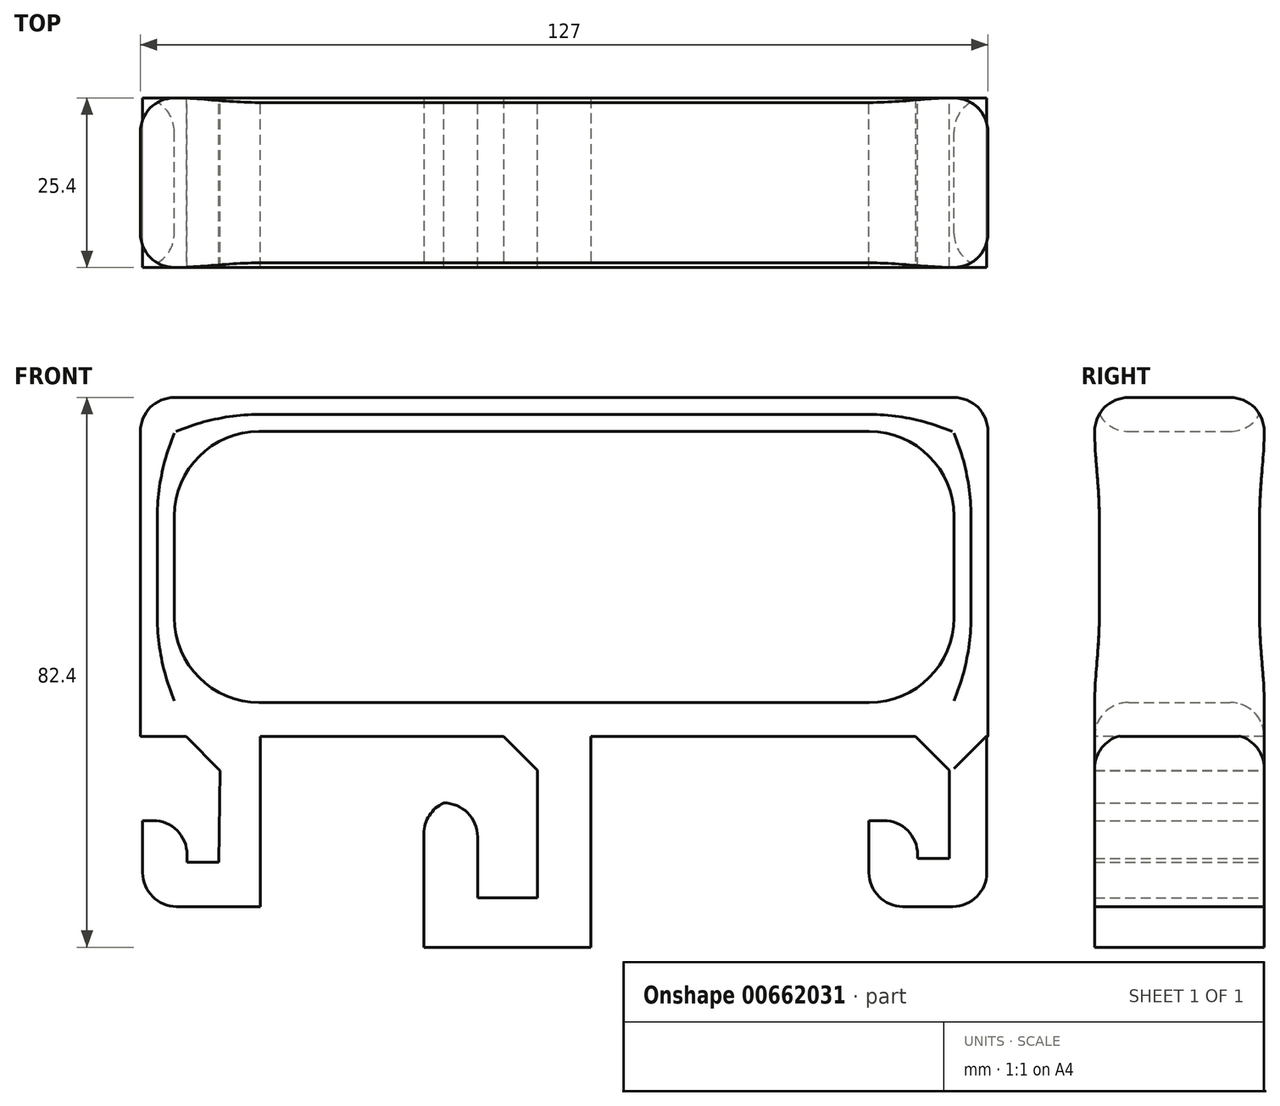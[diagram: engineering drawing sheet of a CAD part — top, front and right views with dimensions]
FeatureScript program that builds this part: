
annotation { "Feature Type Name" : "Feature", "Feature Type Description" : "" }
export const myFeature = defineFeature(function(context is Context, id is Id, definition is map)
    precondition{}
    {
        {
            var Q0;
            Q0=qCreatedBy(makeId("Front.planeOp"),FACE);
            var sketch = newSketch(context, id + "F0", { "sketchPlane" : qUnion([Q0])});
            skLineSegment(sketch, "E0.bottom", {"start": v(-63.5, -25.4) * mm, "end": v(63.5, -25.4) * mm});
            skLineSegment(sketch, "E0.top", {"start": v(-63.5, 25.4) * mm, "end": v(63.5, 25.4) * mm});
            skLineSegment(sketch, "E0.left", {"start": v(-63.5, -25.4) * mm, "end": v(-63.5, 25.4) * mm});
            skLineSegment(sketch, "E0.right", {"start": v(63.5, -25.4) * mm, "end": v(63.5, 25.4) * mm});
            skPoint(sketch, "E0.middle", {"position": v(0, 0) * mm});
            skSolve(sketch);
        }
        {
            var Q0;
            Q0=makeQuery(id+"F0.imprint","IMPRINT",FACE,{"disambiguationData":[TD([[makeQuery(id+"F0.imprint","IMPRINT",EDGE,{"derivedFrom":sQuery(id+"F0.wireOp",EDGE,"E0.bottom")}),1.0]])]});
            extrude(context, id + "F1", {"entities" : qUnion([Q0]), "depth" : 25.4 * mm, "offsetDistance" : 25.4 * mm});
        }
        {
            var Q0;
            Q0=makeQuery(id+"F1.opExtrude","CAP_FACE",FACE,{"disambiguationData":[OSD([sQuery(id+"F0.wireOp",EDGE,"E0.bottom"),sQuery(id+"F0.wireOp",EDGE,"E0.top"),sQuery(id+"F0.wireOp",EDGE,"E0.left"),sQuery(id+"F0.wireOp",EDGE,"E0.right")])],"isStart":true});
            var Q1;
            Q1=makeQuery(id+"F1.opExtrude","CAP_FACE",FACE,{"disambiguationData":[OSD([sQuery(id+"F0.wireOp",EDGE,"E0.bottom"),sQuery(id+"F0.wireOp",EDGE,"E0.top"),sQuery(id+"F0.wireOp",EDGE,"E0.left"),sQuery(id+"F0.wireOp",EDGE,"E0.right")])],"isStart":false});
            shell(context, id + "F2", {"entities" : qUnion([Q0, Q1]), "thickness" : 5.08 * mm});
        }
        {
            var Q0;
            Q0=makeQuery(id+"F2.opShell","OFFSET_EDGE",EDGE,{"disambiguationData":[OSD([sQuery(id+"F0.wireOp",EDGE,"E0.bottom"),sQuery(id+"F0.wireOp",EDGE,"E0.right")])]});
            var Q1;
            Q1=makeQuery(id+"F2.opShell","OFFSET_EDGE",EDGE,{"disambiguationData":[OSD([sQuery(id+"F0.wireOp",EDGE,"E0.top"),sQuery(id+"F0.wireOp",EDGE,"E0.right")])]});
            var Q2;
            Q2=makeQuery(id+"F2.opShell","OFFSET_EDGE",EDGE,{"disambiguationData":[OSD([sQuery(id+"F0.wireOp",EDGE,"E0.bottom"),sQuery(id+"F0.wireOp",EDGE,"E0.left")])]});
            var Q3;
            Q3=makeQuery(id+"F2.opShell","OFFSET_EDGE",EDGE,{"disambiguationData":[OSD([sQuery(id+"F0.wireOp",EDGE,"E0.top"),sQuery(id+"F0.wireOp",EDGE,"E0.left")])]});
            fillet(context, id + "F3", {"entities" : qUnion([Q0, Q1, Q2, Q3]), "radius" : 12.7 * mm, "tangentPropagation" : true, "allowEdgeOverflow" : false});
        }
        {
            var Q0;
            Q0=makeQuery(id+"F1.opExtrude","SWEPT_EDGE",EDGE,{"disambiguationData":[OSD([sQuery(id+"F0.wireOp",EDGE,"E0.top"),sQuery(id+"F0.wireOp",EDGE,"E0.right")])]});
            var Q1;
            Q1=makeQuery(id+"F1.opExtrude","SWEPT_EDGE",EDGE,{"disambiguationData":[OSD([sQuery(id+"F0.wireOp",EDGE,"E0.top"),sQuery(id+"F0.wireOp",EDGE,"E0.left")])]});
            fillet(context, id + "F4", {"entities" : qUnion([Q0, Q1]), "radius" : 5.08 * mm, "tangentPropagation" : true, "allowEdgeOverflow" : false});
        }
        {
            var Q0;
            {var subQ0=sQuery(id+"F0.wireOp",EDGE,"E0.top");Q0=makeQuery(id+"F2.opShell","OFFSET_EDGE",EDGE,{"disambiguationData":[OSD([subQ0]),TDD([makeQuery(id+"F1.opExtrude","CAP_EDGE",EDGE,{"disambiguationData":[OSD([subQ0])],"isStart":true})])]});}
            var Q1;
            Q1=makeQuery(id+"F1.opExtrude","CAP_EDGE",EDGE,{"disambiguationData":[OSD([sQuery(id+"F0.wireOp",EDGE,"E0.top")])],"isStart":true});
            var Q2;
            {var subQ0=sQuery(id+"F0.wireOp",EDGE,"E0.top");Q2=makeQuery(id+"F2.opShell","OFFSET_EDGE",EDGE,{"disambiguationData":[OSD([subQ0]),TDD([makeQuery(id+"F1.opExtrude","CAP_EDGE",EDGE,{"disambiguationData":[OSD([subQ0])],"isStart":false})])]});}
            var Q3;
            Q3=makeQuery(id+"F1.opExtrude","CAP_EDGE",EDGE,{"disambiguationData":[OSD([sQuery(id+"F0.wireOp",EDGE,"E0.top")])],"isStart":false});
            fillet(context, id + "F5", {"entities" : qUnion([Q0, Q1, Q2, Q3]), "radius" : 5.08 * mm, "tangentPropagation" : true, "allowEdgeOverflow" : false});
        }
        {
            var Q0;
            Q0=qCreatedBy(makeId("Front.planeOp"),FACE);
            var sketch = newSketch(context, id + "F6", { "sketchPlane" : qUnion([Q0])});
            skLineSegment(sketch, "E1.bottom", {"start": v(63.32, -25.15) * mm, "end": v(45.68, -25.15) * mm});
            skLineSegment(sketch, "E1.top", {"start": v(63.32, -50.9) * mm, "end": v(45.68, -50.9) * mm});
            skLineSegment(sketch, "E1.left", {"start": v(63.32, -25.15) * mm, "end": v(63.32, -50.9) * mm});
            skLineSegment(sketch, "E1.right", {"start": v(45.68, -25.15) * mm, "end": v(45.68, -50.9) * mm});
            skLineSegment(sketch, "E2.bottom", {"start": v(-63.16, -25.15) * mm, "end": v(-45.52, -25.15) * mm});
            skLineSegment(sketch, "E2.top", {"start": v(-63.16, -50.9) * mm, "end": v(-45.52, -50.9) * mm});
            skLineSegment(sketch, "E2.left", {"start": v(-63.16, -25.15) * mm, "end": v(-63.16, -50.9) * mm});
            skLineSegment(sketch, "E2.right", {"start": v(-45.52, -25.15) * mm, "end": v(-45.52, -50.9) * mm});
            skLineSegment(sketch, "E3", {"start": v(45.68, -50.9) * mm, "end": v(45.68, -38.03) * mm});
            skLineSegment(sketch, "E4", {"start": v(45.68, -38.03) * mm, "end": v(52.97, -38.03) * mm});
            skLineSegment(sketch, "E5", {"start": v(52.97, -38.03) * mm, "end": v(52.97, -43.67) * mm});
            skLineSegment(sketch, "E6", {"start": v(52.97, -43.67) * mm, "end": v(57.71, -43.67) * mm});
            skLineSegment(sketch, "E7", {"start": v(57.71, -43.67) * mm, "end": v(57.71, -25.15) * mm});
            skLineSegment(sketch, "E8", {"start": v(-63.16, -38.03) * mm, "end": v(-56.5, -38.03) * mm});
            skLineSegment(sketch, "E9", {"start": v(-56.5, -38.03) * mm, "end": v(-56.5, -44.26) * mm});
            skLineSegment(sketch, "E10", {"start": v(-56.5, -44.26) * mm, "end": v(-51.76, -44.26) * mm});
            skLineSegment(sketch, "E11", {"start": v(-51.76, -44.26) * mm, "end": v(-49.1, -25.15) * mm});
            skLineSegment(sketch, "E12", {"start": v(-49.1, -25.15) * mm, "end": v(-51.46, -25.15) * mm});
            skLineSegment(sketch, "E13", {"start": v(-51.46, -25.15) * mm, "end": v(-51.76, -44.26) * mm});
            skLineSegment(sketch, "E14", {"start": v(-51.46, -25.15) * mm, "end": v(-45.52, -25.15) * mm});
            skSolve(sketch);
        }
        {
            var Q0;
            {var subQ2=sQuery(id+"F6.wireOp",EDGE,"E2.top");Q0=makeQuery(id+"F6.imprint","IMPRINT",FACE,{"disambiguationData":[TD([[makeQuery(id+"F6.imprint","IMPRINT",EDGE,{"derivedFrom":subQ2}),1.0]])]});}
            var Q1;
            {var subQ0=sQuery(id+"F6.wireOp",EDGE,"E11");Q1=makeQuery(id+"F6.imprint","IMPRINT",FACE,{"disambiguationData":[TD([[makeQuery(id+"F6.imprint","IMPRINT",EDGE,{"derivedFrom":subQ0}),1.0]])]});}
            var Q2;
            Q2=makeQuery(id+"F6.imprint","IMPRINT",FACE,{"disambiguationData":[TD([[makeQuery(id+"F6.imprint","IMPRINT",EDGE,{"derivedFrom":sQuery(id+"F6.wireOp",EDGE,"E1.top")}),-1.0]])]});
            extrude(context, id + "F7", {"entities" : qUnion([Q0, Q1, Q2]), "operationType" : NewBodyOperationType.ADD, "depth" : 25.4 * mm, "offsetDistance" : 25.4 * mm});
        }
        {
            var Q0;
            Q0=makeQuery(id+"F7.opExtrude","CAP_EDGE",EDGE,{"disambiguationData":[OSD([sQuery(id+"F6.wireOp",EDGE,"E1.bottom")])],"isStart":false});
            var Q1;
            Q1=makeQuery(id+"F7.opExtrude","CAP_EDGE",EDGE,{"disambiguationData":[OSD([sQuery(id+"F6.wireOp",EDGE,"E1.bottom")])],"isStart":true});
            fillet(context, id + "F8", {"entities" : qUnion([Q0, Q1]), "radius" : 5.08 * mm, "tangentPropagation" : true, "allowEdgeOverflow" : false});
        }
        {
            var Q0;
            Q0=qCreatedBy(makeId("Front.planeOp"),FACE);
            var sketch = newSketch(context, id + "F9", { "sketchPlane" : qUnion([Q0])});
            skLineSegment(sketch, "E15.bottom", {"start": v(-4.02, -57) * mm, "end": v(4.02, -57) * mm});
            skLineSegment(sketch, "E15.top", {"start": v(-4.02, -21.78) * mm, "end": v(4.02, -21.78) * mm});
            skLineSegment(sketch, "E15.left", {"start": v(-4.02, -57) * mm, "end": v(-4.02, -21.78) * mm});
            skLineSegment(sketch, "E15.right", {"start": v(4.02, -57) * mm, "end": v(4.02, -21.78) * mm});
            skPoint(sketch, "E15.middle", {"position": v(0, -39.39) * mm});
            skLineSegment(sketch, "E16.bottom", {"start": v(4.02, -57) * mm, "end": v(-21, -57) * mm});
            skLineSegment(sketch, "E16.top", {"start": v(4.02, -49.58) * mm, "end": v(-21, -49.58) * mm});
            skLineSegment(sketch, "E16.left", {"start": v(4.02, -57) * mm, "end": v(4.02, -49.58) * mm});
            skLineSegment(sketch, "E16.right", {"start": v(-21, -57) * mm, "end": v(-21, -49.58) * mm});
            skLineSegment(sketch, "E17.bottom", {"start": v(-21, -57) * mm, "end": v(-12.97, -57) * mm});
            skLineSegment(sketch, "E17.top", {"start": v(-21, -35.37) * mm, "end": v(-12.97, -35.37) * mm});
            skLineSegment(sketch, "E17.left", {"start": v(-21, -57) * mm, "end": v(-21, -35.37) * mm});
            skLineSegment(sketch, "E17.right", {"start": v(-12.97, -57) * mm, "end": v(-12.97, -35.37) * mm});
            skSolve(sketch);
        }
        {
            var Q0;
            Q0=qSketchRegion(id+"F9",true);
            extrude(context, id + "F10", {"entities" : qUnion([Q0]), "operationType" : NewBodyOperationType.ADD, "depth" : 25.4 * mm, "offsetDistance" : 25.4 * mm});
        }
        {
            var Q0;
            Q0=makeQuery(id+"F10.opExtrude","CAP_EDGE",EDGE,{"disambiguationData":[OSD([sQuery(id+"F9.wireOp",EDGE,"E15.top")])],"isStart":false});
            var Q1;
            Q1=makeQuery(id+"F10.opExtrude","CAP_EDGE",EDGE,{"disambiguationData":[OSD([sQuery(id+"F9.wireOp",EDGE,"E15.top")])],"isStart":true});
            fillet(context, id + "F11", {"entities" : qUnion([Q0, Q1]), "radius" : 5.08 * mm, "tangentPropagation" : true, "allowEdgeOverflow" : false});
        }
        {
            var Q0;
            Q0=makeQuery(id+"F7.opExtrude","SWEPT_EDGE",EDGE,{"disambiguationData":[OSD([sQuery(id+"F6.wireOp",EDGE,"E8"),sQuery(id+"F6.wireOp",EDGE,"E9")])]});
            var Q1;
            Q1=makeQuery(id+"F10.opExtrude","SWEPT_EDGE",EDGE,{"disambiguationData":[OSD([sQuery(id+"F9.wireOp",EDGE,"E17.top"),sQuery(id+"F9.wireOp",EDGE,"E17.right")])]});
            var Q2;
            Q2=makeQuery(id+"F7.opExtrude","SWEPT_EDGE",EDGE,{"disambiguationData":[OSD([sQuery(id+"F6.wireOp",EDGE,"E4"),sQuery(id+"F6.wireOp",EDGE,"E5")])]});
            fillet(context, id + "F12", {"entities" : qUnion([Q0, Q1, Q2]), "radius" : 5.08 * mm, "tangentPropagation" : true, "allowEdgeOverflow" : false});
        }
        {
            var Q0;
            Q0=makeQuery(id+"F7.boolean.opBoolean","INTERSECT",EDGE,{"derivedFrom":[makeQuery(id+"F1.opExtrude","SWEPT_FACE",FACE,{"disambiguationData":[OSD([sQuery(id+"F0.wireOp",EDGE,"E0.bottom")])]}),makeQuery(id+"F7.opExtrude","SWEPT_FACE",FACE,{"disambiguationData":[OSD([sQuery(id+"F6.wireOp",EDGE,"E7")])]})]});
            var Q1;
            {var subQ5=sQuery(id+"F6.wireOp",EDGE,"E2.right");var subQ8=sQuery(id+"F0.wireOp",EDGE,"E0.bottom");Q1=makeQuery(id+"F10.boolean.opBoolean","INTERSECT",EDGE,{"derivedFrom":[makeQuery(id+"F7.boolean.opBoolean","SPLIT",FACE,{"disambiguationData":[TD([makeQuery(id+"F7.opExtrude","SWEPT_FACE",FACE,{"disambiguationData":[OSD([subQ5])]})])],"derivedFrom":makeQuery(id+"F1.opExtrude","SWEPT_FACE",FACE,{"disambiguationData":[OSD([subQ8])]})}),makeQuery(id+"F10.opExtrude","SWEPT_FACE",FACE,{"disambiguationData":[OSD([sQuery(id+"F9.wireOp",EDGE,"E15.left")])]})]});}
            var Q2;
            Q2=makeQuery(id+"F7.boolean.opBoolean","INTERSECT",EDGE,{"derivedFrom":[makeQuery(id+"F1.opExtrude","SWEPT_FACE",FACE,{"disambiguationData":[OSD([sQuery(id+"F0.wireOp",EDGE,"E0.bottom")])]}),makeQuery(id+"F7.opExtrude","SWEPT_FACE",FACE,{"disambiguationData":[OSD([sQuery(id+"F6.wireOp",EDGE,"E13")])]})]});
            chamfer(context, id + "F13", {"entities" : qUnion([Q0, Q1, Q2]), "width" : 5.08 * mm, "tangentPropagation" : true});
        }
        {
            var Q0;
            Q0=makeQuery(id+"F7.opExtrude","SWEPT_EDGE",EDGE,{"disambiguationData":[OSD([sQuery(id+"F6.wireOp",EDGE,"E2.top"),sQuery(id+"F6.wireOp",EDGE,"E2.left")])]});
            var Q1;
            Q1=makeQuery(id+"F10.opExtrude","SWEPT_EDGE",EDGE,{"disambiguationData":[OSD([sQuery(id+"F9.wireOp",EDGE,"E17.bottom"),sQuery(id+"F9.wireOp",EDGE,"E17.left")])]});
            var Q2;
            Q2=makeQuery(id+"F7.opExtrude","SWEPT_EDGE",EDGE,{"disambiguationData":[OSD([sQuery(id+"F6.wireOp",EDGE,"E1.top"),sQuery(id+"F6.wireOp",EDGE,"E3")])]});
            fillet(context, id + "F14", {"entities" : qUnion([Q0, Q1, Q2]), "radius" : 5.08 * mm, "tangentPropagation" : true, "allowEdgeOverflow" : false});
        }
    });
